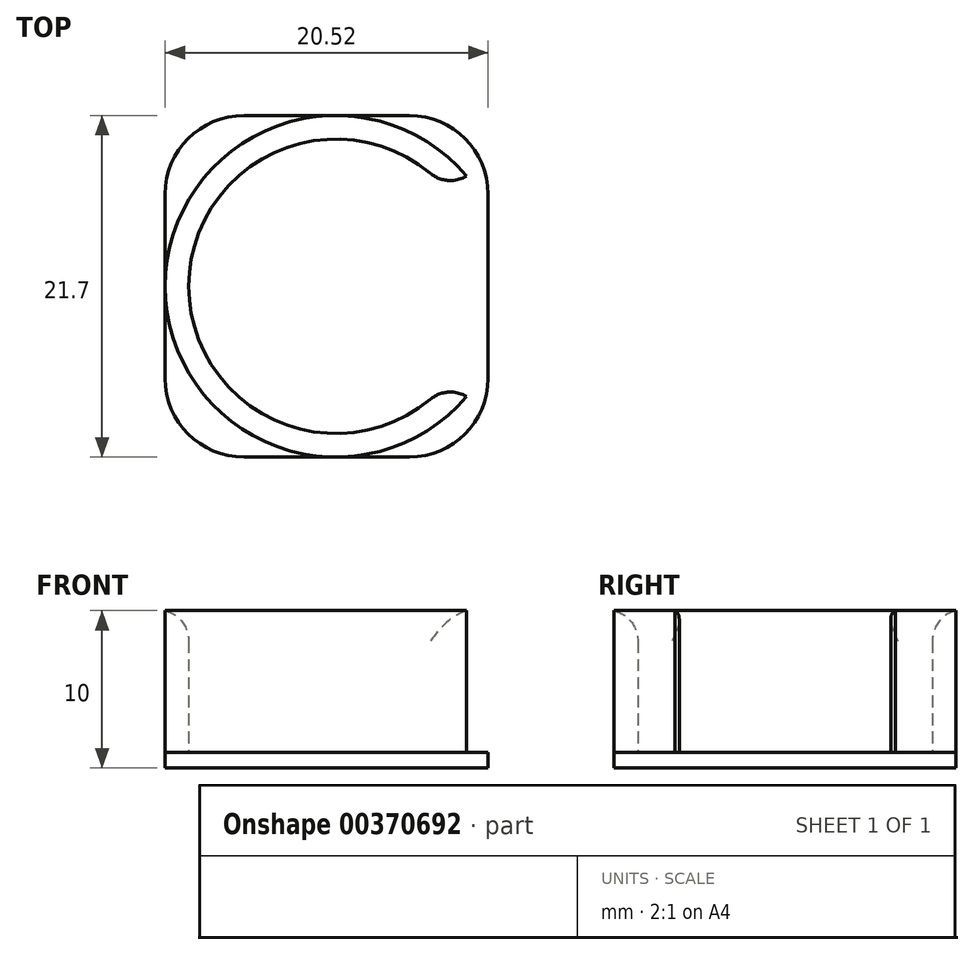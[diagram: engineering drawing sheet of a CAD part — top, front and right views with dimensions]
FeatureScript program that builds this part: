
annotation { "Feature Type Name" : "Feature", "Feature Type Description" : "" }
export const myFeature = defineFeature(function(context is Context, id is Id, definition is map)
    precondition{}
    {
        {
            var Q0;
            Q0=qCreatedBy(makeId("Top.planeOp"),FACE);
            var sketch = newSketch(context, id + "F0", { "sketchPlane" : qUnion([Q0])});
            skArc(sketch, "E0", {"start": v(7.56, 5.5) * mm, "mid": v(-9.35, 0) * mm, "end": v(7.56, -5.5) * mm});
            skLineSegment(sketch, "E1.direction1", {"start": v(0, 0) * mm, "end": v(19.5, 0) * mm, "construction": true});
            skArc(sketch, "E2.1", {"start": v(8.29, 7) * mm, "mid": v(-10.85, 0) * mm, "end": v(8.29, -7) * mm});
            skLineSegment(sketch, "E3", {"start": v(7.56, 5.5) * mm, "end": v(8.29, 7) * mm});
            skLineSegment(sketch, "E4", {"start": v(7.56, -5.5) * mm, "end": v(8.29, -7) * mm});
            skSolve(sketch);
        }
        {
            var Q0;
            Q0=qCreatedBy(makeId("Top.planeOp"),FACE);
            var sketch = newSketch(context, id + "F1", { "sketchPlane" : qUnion([Q0])});
            skArc(sketch, "E5", {"start": v(7.52, 5.55) * mm, "mid": v(-9.35, 0) * mm, "end": v(7.52, -5.55) * mm});
            skArc(sketch, "E6.2.0.0", {"start": v(29.28, -5.55) * mm, "mid": v(36.8, -9.35) * mm, "end": v(44.32, -5.55) * mm});
            skLineSegment(sketch, "E6.direction1", {"start": v(0, 0) * mm, "end": v(18.5, 0) * mm, "construction": true});
            skArc(sketch, "E7.0", {"start": v(8.15, 7.16) * mm, "mid": v(-10.85, 0) * mm, "end": v(8.15, -7.16) * mm});
            skArc(sketch, "E8.0", {"start": v(28.65, -7.16) * mm, "mid": v(36.8, -10.85) * mm, "end": v(44.95, -7.16) * mm});
            skLineSegment(sketch, "E9", {"start": v(8.15, 7.16) * mm, "end": v(10.25, 7.16) * mm});
            skLineSegment(sketch, "E10.1.0.0", {"start": v(26.55, 7.16) * mm, "end": v(28.65, 7.16) * mm});
            skLineSegment(sketch, "E10.direction1", {"start": v(8.15, 7.16) * mm, "end": v(10.25, 7.16) * mm, "construction": true});
            skLineSegment(sketch, "E11", {"start": v(9.2, 5.55) * mm, "end": v(7.52, 5.55) * mm});
            skLineSegment(sketch, "E12", {"start": v(7.52, 5.55) * mm, "end": v(10.88, 5.55) * mm});
            skLineSegment(sketch, "E13.MirrorCS", {"start": v(8.15, -7.16) * mm, "end": v(10.25, -7.16) * mm});
            skLineSegment(sketch, "E14.MirrorCS", {"start": v(7.52, -5.55) * mm, "end": v(10.88, -5.55) * mm});
            skLineSegment(sketch, "E15.MirrorCS", {"start": v(26.55, -7.16) * mm, "end": v(28.65, -7.16) * mm});
            skLineSegment(sketch, "E16.MirrorCS", {"start": v(25.68, -5.55) * mm, "end": v(29.28, -5.55) * mm});
            skArc(sketch, "E17.trimOffspring", {"start": v(10.25, -7.16) * mm, "mid": v(18.4, -10.93) * mm, "end": v(26.55, -7.16) * mm});
            skArc(sketch, "E18.trimOffspring", {"start": v(10.88, -5.55) * mm, "mid": v(18.28, -9.29) * mm, "end": v(25.68, -5.55) * mm});
            skArc(sketch, "E19.trimOffspring", {"start": v(26.55, 7.16) * mm, "mid": v(18.4, 10.93) * mm, "end": v(10.25, 7.16) * mm});
            skArc(sketch, "E20.trimOffspring", {"start": v(25.68, 5.55) * mm, "mid": v(18.28, 9.29) * mm, "end": v(10.88, 5.55) * mm});
            skLineSegment(sketch, "E21", {"start": v(25.68, 5.55) * mm, "end": v(29.28, 5.55) * mm});
            skArc(sketch, "E22", {"start": v(62.82, 5.55) * mm, "mid": v(55.3, 9.35) * mm, "end": v(47.78, 5.55) * mm});
            skArc(sketch, "E23.2.0.0", {"start": v(84.58, -5.55) * mm, "mid": v(101.45, 0) * mm, "end": v(84.58, 5.55) * mm});
            skLineSegment(sketch, "E23.direction1", {"start": v(55.3, 0) * mm, "end": v(73.8, 0) * mm, "construction": true});
            skArc(sketch, "E24.0", {"start": v(63.45, 7.16) * mm, "mid": v(55.3, 10.85) * mm, "end": v(47.15, 7.16) * mm});
            skArc(sketch, "E25.0", {"start": v(83.95, -7.16) * mm, "mid": v(102.95, 0) * mm, "end": v(83.95, 7.16) * mm});
            skLineSegment(sketch, "E26", {"start": v(63.45, 7.16) * mm, "end": v(65.55, 7.16) * mm});
            skLineSegment(sketch, "E27.1.0.0", {"start": v(81.85, 7.16) * mm, "end": v(83.95, 7.16) * mm});
            skLineSegment(sketch, "E27.direction1", {"start": v(63.45, 7.16) * mm, "end": v(65.55, 7.16) * mm, "construction": true});
            skLineSegment(sketch, "E28", {"start": v(64.5, 5.55) * mm, "end": v(62.82, 5.55) * mm});
            skLineSegment(sketch, "E29", {"start": v(62.82, 5.55) * mm, "end": v(66.18, 5.55) * mm});
            skLineSegment(sketch, "E30.MirrorCS", {"start": v(63.45, -7.16) * mm, "end": v(65.55, -7.16) * mm});
            skLineSegment(sketch, "E31.MirrorCS", {"start": v(62.82, -5.55) * mm, "end": v(66.18, -5.55) * mm});
            skLineSegment(sketch, "E32.MirrorCS", {"start": v(81.85, -7.16) * mm, "end": v(83.95, -7.16) * mm});
            skLineSegment(sketch, "E33.MirrorCS", {"start": v(80.98, -5.55) * mm, "end": v(84.58, -5.55) * mm});
            skArc(sketch, "E34.trimOffspring", {"start": v(65.55, -7.16) * mm, "mid": v(73.7, -10.93) * mm, "end": v(81.85, -7.16) * mm});
            skArc(sketch, "E35.trimOffspring", {"start": v(66.18, -5.55) * mm, "mid": v(73.58, -9.29) * mm, "end": v(80.98, -5.55) * mm});
            skArc(sketch, "E36.trimOffspring", {"start": v(81.85, 7.16) * mm, "mid": v(73.7, 10.93) * mm, "end": v(65.55, 7.16) * mm});
            skArc(sketch, "E37.trimOffspring", {"start": v(80.98, 5.55) * mm, "mid": v(73.58, 9.29) * mm, "end": v(66.18, 5.55) * mm});
            skLineSegment(sketch, "E38", {"start": v(80.98, 5.55) * mm, "end": v(84.58, 5.55) * mm});
            skLineSegment(sketch, "E39.0.3.0", {"start": v(63.35, 7.16) * mm, "end": v(65.45, 7.16) * mm});
            skLineSegment(sketch, "E40", {"start": v(44.95, 7.16) * mm, "end": v(47.15, 7.16) * mm});
            skLineSegment(sketch, "E41", {"start": v(44.95, -7.16) * mm, "end": v(47.15, -7.16) * mm});
            skLineSegment(sketch, "E42", {"start": v(44.32, -5.55) * mm, "end": v(47.78, -5.55) * mm});
            skLineSegment(sketch, "E43", {"start": v(44.32, 5.55) * mm, "end": v(47.78, 5.55) * mm});
            skPoint(sketch, "E43.startSnap0", {"position": v(27.48, 5.55) * mm});
            skArc(sketch, "E44.trimOffspring", {"start": v(44.95, 7.16) * mm, "mid": v(36.8, 10.85) * mm, "end": v(28.65, 7.16) * mm});
            skArc(sketch, "E45.trimOffspring", {"start": v(46.05, 5.67) * mm, "mid": v(46.01, 5.61) * mm, "end": v(45.98, 5.55) * mm});
            skArc(sketch, "E46.trimOffspring", {"start": v(46.12, 5.55) * mm, "mid": v(46.09, 5.61) * mm, "end": v(46.05, 5.67) * mm});
            skArc(sketch, "E47.trimOffspring", {"start": v(47.78, -5.55) * mm, "mid": v(55.3, -9.35) * mm, "end": v(62.82, -5.55) * mm});
            skArc(sketch, "E48.trimOffspring", {"start": v(44.32, 5.55) * mm, "mid": v(36.8, 9.35) * mm, "end": v(29.28, 5.55) * mm});
            skArc(sketch, "E49.trimOffspring", {"start": v(45.98, -5.55) * mm, "mid": v(46.01, -5.61) * mm, "end": v(46.05, -5.67) * mm});
            skArc(sketch, "E50.trimOffspring", {"start": v(46.05, -5.67) * mm, "mid": v(46.09, -5.61) * mm, "end": v(46.12, -5.55) * mm});
            skArc(sketch, "E51.trimOffspring", {"start": v(47.15, -7.16) * mm, "mid": v(55.3, -10.85) * mm, "end": v(63.45, -7.16) * mm});
            skSolve(sketch);
        }
        {
            var Q0;
            Q0=makeQuery(id+"F0.imprint","IMPRINT",FACE,{"disambiguationData":[TD([[makeQuery(id+"F0.imprint","IMPRINT",EDGE,{"derivedFrom":sQuery(id+"F0.wireOp",EDGE,"E0")}),-1.0]])]});
            extrude(context, id + "F2", {"entities" : qUnion([Q0]), "depth" : 10 * mm, "offsetDistance" : 25 * mm});
        }
        {
            var Q0;
            Q0=qCreatedBy(makeId("Top.planeOp"),FACE);
            var sketch = newSketch(context, id + "F3", { "sketchPlane" : qUnion([Q0])});
            skLineSegment(sketch, "E52.bottom", {"start": v(-10.85, -10.85) * mm, "end": v(9.67, -10.85) * mm});
            skLineSegment(sketch, "E52.top", {"start": v(-10.85, 10.85) * mm, "end": v(9.67, 10.85) * mm});
            skLineSegment(sketch, "E52.left", {"start": v(-10.85, -10.85) * mm, "end": v(-10.85, 10.85) * mm});
            skLineSegment(sketch, "E52.right", {"start": v(9.67, -10.85) * mm, "end": v(9.67, 10.85) * mm});
            skPoint(sketch, "E52.middle", {"position": v(-0.6, 0) * mm});
            skCircle(sketch, "E53", {"center": v(0, 0) * mm, "radius": 9.37 * mm, "construction": true});
            skSolve(sketch);
        }
        {
            var Q0;
            Q0=makeQuery(id+"F3.imprint","IMPRINT",FACE,{"disambiguationData":[TD([[makeQuery(id+"F3.imprint","IMPRINT",EDGE,{"derivedFrom":sQuery(id+"F3.wireOp",EDGE,"E52.bottom")}),1.0]])]});
            extrude(context, id + "F4", {"entities" : qUnion([Q0]), "operationType" : NewBodyOperationType.ADD, "depth" : 1 * mm, "offsetDistance" : 25 * mm});
        }
        {
            var Q0;
            Q0=makeQuery(id+"F4.opExtrude","SWEPT_EDGE",EDGE,{"disambiguationData":[OSD([sQuery(id+"F3.wireOp",EDGE,"E52.bottom"),sQuery(id+"F3.wireOp",EDGE,"E52.left")])]});
            var Q1;
            Q1=makeQuery(id+"F4.opExtrude","SWEPT_EDGE",EDGE,{"disambiguationData":[OSD([sQuery(id+"F3.wireOp",EDGE,"E52.bottom"),sQuery(id+"F3.wireOp",EDGE,"E52.right")])]});
            var Q2;
            Q2=makeQuery(id+"F4.opExtrude","SWEPT_EDGE",EDGE,{"disambiguationData":[OSD([sQuery(id+"F3.wireOp",EDGE,"E52.top"),sQuery(id+"F3.wireOp",EDGE,"E52.left")])]});
            var Q3;
            Q3=makeQuery(id+"F4.opExtrude","SWEPT_EDGE",EDGE,{"disambiguationData":[OSD([sQuery(id+"F3.wireOp",EDGE,"E52.top"),sQuery(id+"F3.wireOp",EDGE,"E52.right")])]});
            fillet(context, id + "F5", {"entities" : qUnion([Q0, Q1, Q2, Q3]), "radius" : 5 * mm, "tangentPropagation" : true, "allowEdgeOverflow" : false});
        }
        {
            var Q0;
            Q0=qCreatedBy(makeId("Right.planeOp"),FACE);
            var sketch = newSketch(context, id + "F6", { "sketchPlane" : qUnion([Q0])});
            skLineSegment(sketch, "E54.bottom", {"start": v(-5.5, 1) * mm, "end": v(5.5, 1) * mm});
            skLineSegment(sketch, "E54.top", {"start": v(-5.5, 51) * mm, "end": v(5.5, 51) * mm});
            skLineSegment(sketch, "E54.left", {"start": v(-5.5, 1) * mm, "end": v(-5.5, 51) * mm});
            skLineSegment(sketch, "E54.right", {"start": v(5.5, 1) * mm, "end": v(5.5, 51) * mm});
            skPoint(sketch, "E54.middle", {"position": v(0, 26) * mm});
            skSolve(sketch);
        }
        {
            var Q0;
            Q0=makeQuery(id+"F2.opExtrude","CAP_EDGE",EDGE,{"disambiguationData":[OSD([sQuery(id+"F0.wireOp",EDGE,"E0")])],"isStart":false});
            var Q1;
            Q1=makeQuery(id+"F2.opExtrude","SWEPT_EDGE",EDGE,{"disambiguationData":[OSD([sQuery(id+"F0.wireOp",EDGE,"E0"),sQuery(id+"F0.wireOp",EDGE,"E3")])]});
            var Q2;
            Q2=makeQuery(id+"F2.opExtrude","SWEPT_EDGE",EDGE,{"disambiguationData":[OSD([sQuery(id+"F0.wireOp",EDGE,"E0"),sQuery(id+"F0.wireOp",EDGE,"E4")])]});
            fillet(context, id + "F7", {"entities" : qUnion([Q0, Q1, Q2]), "radius" : 2 * mm, "tangentPropagation" : true, "allowEdgeOverflow" : false});
        }
    });
